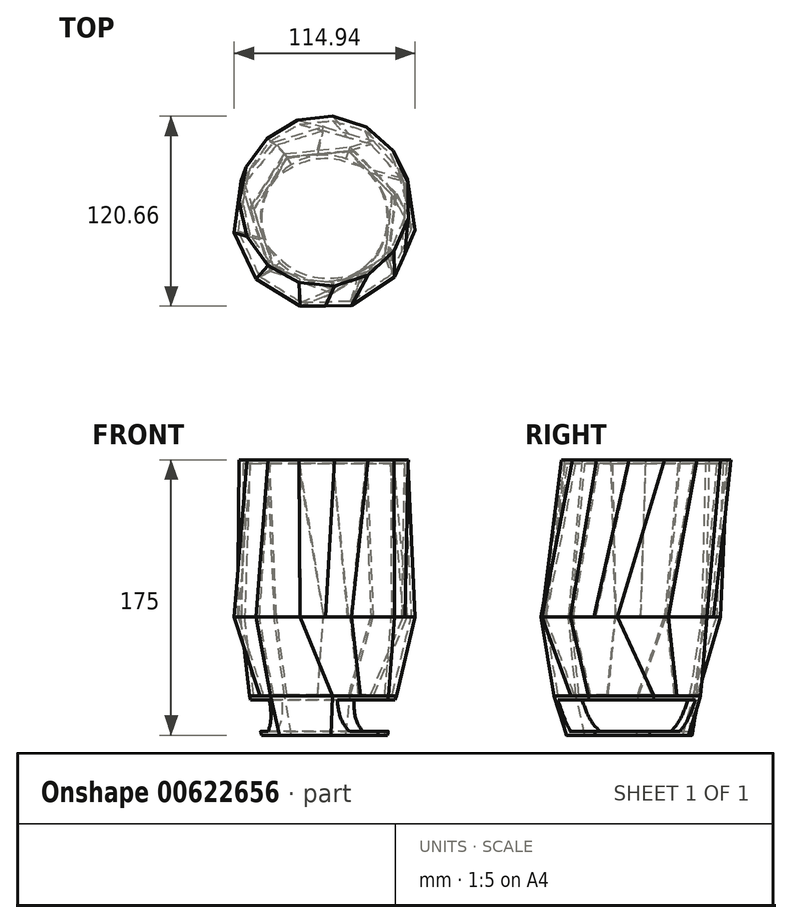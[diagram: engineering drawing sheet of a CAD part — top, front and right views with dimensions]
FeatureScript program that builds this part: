
annotation { "Feature Type Name" : "Feature", "Feature Type Description" : "" }
export const myFeature = defineFeature(function(context is Context, id is Id, definition is map)
    precondition{}
    {
        {
            var Q0;
            Q0=qCreatedBy(makeId("Top.planeOp"),FACE);
            var sketch = newSketch(context, id + "F0", { "sketchPlane" : qUnion([Q0])});
            skCircle(sketch, "E0", {"center": v(0, 0) * mm, "radius": 40 * mm});
            skSolve(sketch);
        }
        {
            var Q0;
            Q0=qCreatedBy(makeId("Top.planeOp"),FACE);
            cPlane(context, id + "F1", {"entities" : qUnion([Q0]), "cplaneType" : CPlaneType.OFFSET, "offset" : 25 * mm, "width" : 150 * mm, "height" : 150 * mm});
        }
        {
            var Q0;
            Q0=qCreatedBy(id+"F1.planeOp",FACE);
            var sketch = newSketch(context, id + "F2", { "sketchPlane" : qUnion([Q0])});
            skCircle(sketch, "E1.cCircle", {"center": v(0, 0) * mm, "radius": 48.14 * mm, "construction": true});
            skLineSegment(sketch, "E1.0", {"start": v(-25.3, 40.96) * mm, "end": v(16.25, 45.32) * mm});
            skLineSegment(sketch, "E1.1", {"start": v(16.25, 45.32) * mm, "end": v(45.56, 15.55) * mm});
            skLineSegment(sketch, "E1.2", {"start": v(45.56, 15.55) * mm, "end": v(40.57, -25.93) * mm});
            skLineSegment(sketch, "E1.3", {"start": v(40.57, -25.93) * mm, "end": v(5.02, -47.88) * mm});
            skLineSegment(sketch, "E1.4", {"start": v(5.02, -47.88) * mm, "end": v(-34.3, -33.78) * mm});
            skLineSegment(sketch, "E1.5", {"start": v(-34.3, -33.78) * mm, "end": v(-47.8, 5.76) * mm});
            skLineSegment(sketch, "E1.6", {"start": v(-47.8, 5.76) * mm, "end": v(-25.3, 40.96) * mm});
            skSolve(sketch);
        }
        {
            var Q0;
            Q0 = qSketchRegion(id + "F0", true);
            var Q1;
            Q1 = qSketchRegion(id + "F2", true);
            loft(context, id + "F3", {"sheetProfilesArray" : [{ "sheetProfileEntities" : qUnion([Q0]) }, { "sheetProfileEntities" : qUnion([Q1]) }]});
        }
        {
            var Q0;
            Q0=makeQuery(id+"F3.opLoft","SWEPT_FACE",FACE,{"disambiguationData":[OSD([sQuery(id+"F0.wireOp",EDGE,"E0"),sQuery(id+"F2.wireOp",EDGE,"E1.1"),sQuery(id+"F2.wireOp",EDGE,"E1.2"),sQuery(id+"F2.wireOp",EDGE,"E1.3"),sQuery(id+"F2.wireOp",EDGE,"E1.4")])]});
            var Q1;
            Q1=makeQuery(id+"F3.opLoft","SWEPT_FACE",FACE,{"disambiguationData":[OSD([sQuery(id+"F0.wireOp",EDGE,"E0"),sQuery(id+"F2.wireOp",EDGE,"E1.0"),sQuery(id+"F2.wireOp",EDGE,"E1.1"),sQuery(id+"F2.wireOp",EDGE,"E1.2"),sQuery(id+"F2.wireOp",EDGE,"E1.6")])]});
            var Q2;
            Q2=makeQuery(id+"F3.opLoft","SWEPT_FACE",FACE,{"disambiguationData":[OSD([sQuery(id+"F0.wireOp",EDGE,"E0"),sQuery(id+"F2.wireOp",EDGE,"E1.0"),sQuery(id+"F2.wireOp",EDGE,"E1.4"),sQuery(id+"F2.wireOp",EDGE,"E1.5"),sQuery(id+"F2.wireOp",EDGE,"E1.6")])]});
            var Q3;
            Q3=makeQuery(id+"F3.opLoft","SWEPT_FACE",FACE,{"disambiguationData":[OSD([sQuery(id+"F0.wireOp",EDGE,"E0"),sQuery(id+"F2.wireOp",EDGE,"E1.2"),sQuery(id+"F2.wireOp",EDGE,"E1.3"),sQuery(id+"F2.wireOp",EDGE,"E1.4"),sQuery(id+"F2.wireOp",EDGE,"E1.5")])]});
            shell(context, id + "F4", {"entities" : qUnion([Q0, Q1, Q2, Q3]), "thickness" : 2.5 * mm});
        }
        {
            var Q0;
            Q0=qCreatedBy(id+"F1.planeOp",FACE);
            cPlane(context, id + "F5", {"entities" : qUnion([Q0]), "cplaneType" : CPlaneType.OFFSET, "offset" : 50 * mm, "width" : 150 * mm, "height" : 150 * mm});
        }
        {
            var Q0;
            Q0=qCreatedBy(id+"F5.planeOp",FACE);
            var sketch = newSketch(context, id + "F6", { "sketchPlane" : qUnion([Q0])});
            skCircle(sketch, "E2.cCircle", {"center": v(0, 0) * mm, "radius": 58.06 * mm, "construction": true});
            skLineSegment(sketch, "E2.0", {"start": v(57.57, -7.54) * mm, "end": v(44.36, -37.47) * mm});
            skLineSegment(sketch, "E2.1", {"start": v(44.36, -37.47) * mm, "end": v(17.06, -55.5) * mm});
            skLineSegment(sketch, "E2.2", {"start": v(17.06, -55.5) * mm, "end": v(-15.66, -55.91) * mm});
            skLineSegment(sketch, "E2.3", {"start": v(-15.66, -55.91) * mm, "end": v(-43.4, -38.57) * mm});
            skLineSegment(sketch, "E2.4", {"start": v(-43.4, -38.57) * mm, "end": v(-57.37, -8.98) * mm});
            skLineSegment(sketch, "E2.5", {"start": v(-57.37, -8.98) * mm, "end": v(-53.12, 23.46) * mm});
            skLineSegment(sketch, "E2.6", {"start": v(-53.12, 23.46) * mm, "end": v(-32, 48.45) * mm});
            skLineSegment(sketch, "E2.7", {"start": v(-32, 48.45) * mm, "end": v(-0.73, 58.06) * mm});
            skLineSegment(sketch, "E2.8", {"start": v(-0.73, 58.06) * mm, "end": v(30.78, 49.24) * mm});
            skLineSegment(sketch, "E2.9", {"start": v(30.78, 49.24) * mm, "end": v(52.51, 24.78) * mm});
            skLineSegment(sketch, "E2.10", {"start": v(52.51, 24.78) * mm, "end": v(57.57, -7.54) * mm});
            skSolve(sketch);
        }
        {
            var Q1;
            Q1=makeQuery(id+"F3.opLoft","CAP_FACE",FACE,{"disambiguationData":[OSD([makeQuery(id+"F2.imprint","IMPRINT",FACE,{"disambiguationData":[TD([[makeQuery(id+"F2.imprint","IMPRINT",EDGE,{"derivedFrom":sQuery(id+"F2.wireOp",EDGE,"E1.0")}),-1.0]])]})])],"isStart":true});
            var Q2;
            Q2=makeQuery(id+"F6.imprint","IMPRINT",FACE,{"disambiguationData":[TD([[makeQuery(id+"F6.imprint","IMPRINT",EDGE,{"derivedFrom":sQuery(id+"F6.wireOp",EDGE,"E2.0")}),-1.0]])]});
            loft(context, id + "F7", {"operationType" : NewBodyOperationType.ADD, "sheetProfilesArray" : [{ "sheetProfileEntities" : qUnion([Q1]) }, { "sheetProfileEntities" : qUnion([Q2]) }]});
        }
        {
            var Q0;
            Q0=qCreatedBy(id+"F5.planeOp",FACE);
            cPlane(context, id + "F8", {"entities" : qUnion([Q0]), "cplaneType" : CPlaneType.OFFSET, "offset" : 100 * mm, "width" : 150 * mm, "height" : 150 * mm});
        }
        {
            var Q0;
            Q0=qCreatedBy(id+"F8.planeOp",FACE);
            var sketch = newSketch(context, id + "F9", { "sketchPlane" : qUnion([Q0])});
            skCircle(sketch, "E3.cCircle", {"center": v(0, 10.75) * mm, "radius": 54.25 * mm, "construction": true});
            skLineSegment(sketch, "E3.0", {"start": v(-36.69, 50.72) * mm, "end": v(-17.26, 62.18) * mm});
            skLineSegment(sketch, "E3.1", {"start": v(-17.26, 62.18) * mm, "end": v(5.16, 64.75) * mm});
            skLineSegment(sketch, "E3.2", {"start": v(5.16, 64.75) * mm, "end": v(26.68, 57.99) * mm});
            skLineSegment(sketch, "E3.3", {"start": v(26.68, 57.99) * mm, "end": v(43.59, 43.05) * mm});
            skLineSegment(sketch, "E3.4", {"start": v(43.59, 43.05) * mm, "end": v(52.96, 22.53) * mm});
            skLineSegment(sketch, "E3.5", {"start": v(52.96, 22.53) * mm, "end": v(53.17, -0.03) * mm});
            skLineSegment(sketch, "E3.6", {"start": v(53.17, -0.03) * mm, "end": v(44.2, -20.72) * mm});
            skLineSegment(sketch, "E3.7", {"start": v(44.2, -20.72) * mm, "end": v(27.57, -35.98) * mm});
            skLineSegment(sketch, "E3.8", {"start": v(27.57, -35.98) * mm, "end": v(6.19, -43.15) * mm});
            skLineSegment(sketch, "E3.9", {"start": v(6.19, -43.15) * mm, "end": v(-16.27, -41.01) * mm});
            skLineSegment(sketch, "E3.10", {"start": v(-16.27, -41.01) * mm, "end": v(-35.92, -29.92) * mm});
            skLineSegment(sketch, "E3.11", {"start": v(-35.92, -29.92) * mm, "end": v(-49.35, -11.8) * mm});
            skLineSegment(sketch, "E3.12", {"start": v(-49.35, -11.8) * mm, "end": v(-54.25, 10.23) * mm});
            skLineSegment(sketch, "E3.13", {"start": v(-54.25, 10.23) * mm, "end": v(-49.77, 32.34) * mm});
            skLineSegment(sketch, "E3.14", {"start": v(-49.77, 32.34) * mm, "end": v(-36.69, 50.72) * mm});
            skSolve(sketch);
        }
        {
            var Q1;
            Q1=makeQuery(id+"F9.imprint","IMPRINT",FACE,{"disambiguationData":[TD([[makeQuery(id+"F9.imprint","IMPRINT",EDGE,{"derivedFrom":sQuery(id+"F9.wireOp",EDGE,"E3.0")}),-1.0]])]});
            var Q2;
            Q2=makeQuery(id+"F7.opLoft","CAP_FACE",FACE,{"disambiguationData":[OSD([makeQuery(id+"F6.imprint","IMPRINT",FACE,{"disambiguationData":[TD([[makeQuery(id+"F6.imprint","IMPRINT",EDGE,{"derivedFrom":sQuery(id+"F6.wireOp",EDGE,"E2.0")}),-1.0]])]})])],"isStart":true});
            loft(context, id + "F10", {"operationType" : NewBodyOperationType.ADD, "sheetProfilesArray" : [{ "sheetProfileEntities" : qUnion([Q1]) }, { "sheetProfileEntities" : qUnion([Q2]) }]});
        }
        {
            var Q0;
            Q0=makeQuery(id+"F3.opLoft","CAP_FACE",FACE,{"disambiguationData":[OSD([makeQuery(id+"F0.imprint","IMPRINT",FACE,{"disambiguationData":[TD([[makeQuery(id+"F0.imprint","IMPRINT",EDGE,{"derivedFrom":sQuery(id+"F0.wireOp",EDGE,"E0")}),1.0]])]})])],"isStart":true});
            shell(context, id + "F11", {"entities" : qUnion([Q0]), "thickness" : 2.5 * mm});
        }
    });
